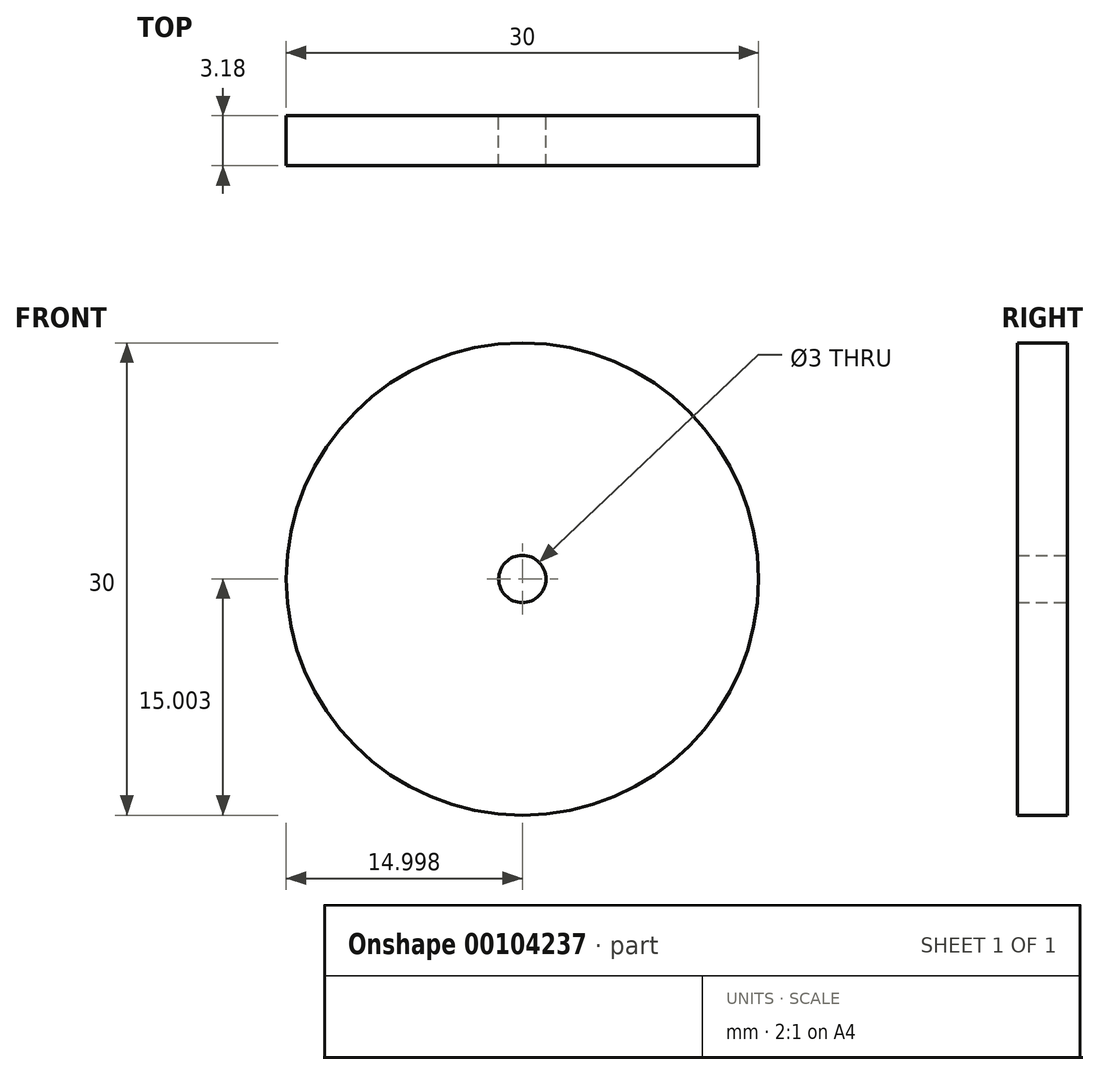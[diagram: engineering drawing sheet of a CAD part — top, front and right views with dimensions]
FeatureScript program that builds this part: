
annotation { "Feature Type Name" : "Feature", "Feature Type Description" : "" }
export const myFeature = defineFeature(function(context is Context, id is Id, definition is map)
    precondition{}
    {
        {
            var Q0;
            Q0=qCreatedBy(makeId("Front.planeOp"),FACE);
            var sketch = newSketch(context, id + "F0", { "sketchPlane" : qUnion([Q0])});
            skCircle(sketch, "E0", {"center": v(-30.55, 36.75) * mm, "radius": 15 * mm});
            skCircle(sketch, "E1", {"center": v(-30.55, 36.75) * mm, "radius": 1.5 * mm});
            skSolve(sketch);
        }
        {
            var Q0;
            Q0=makeQuery(id+"F0.imprint","IMPRINT",FACE,{"disambiguationData":[TD([[makeQuery(id+"F0.imprint","IMPRINT",EDGE,{"derivedFrom":sQuery(id+"F0.wireOp",EDGE,"E0")}),1.0]])]});
            extrude(context, id + "F1", {"entities" : qUnion([Q0]), "depth" : 3.17 * mm});
        }
    });
